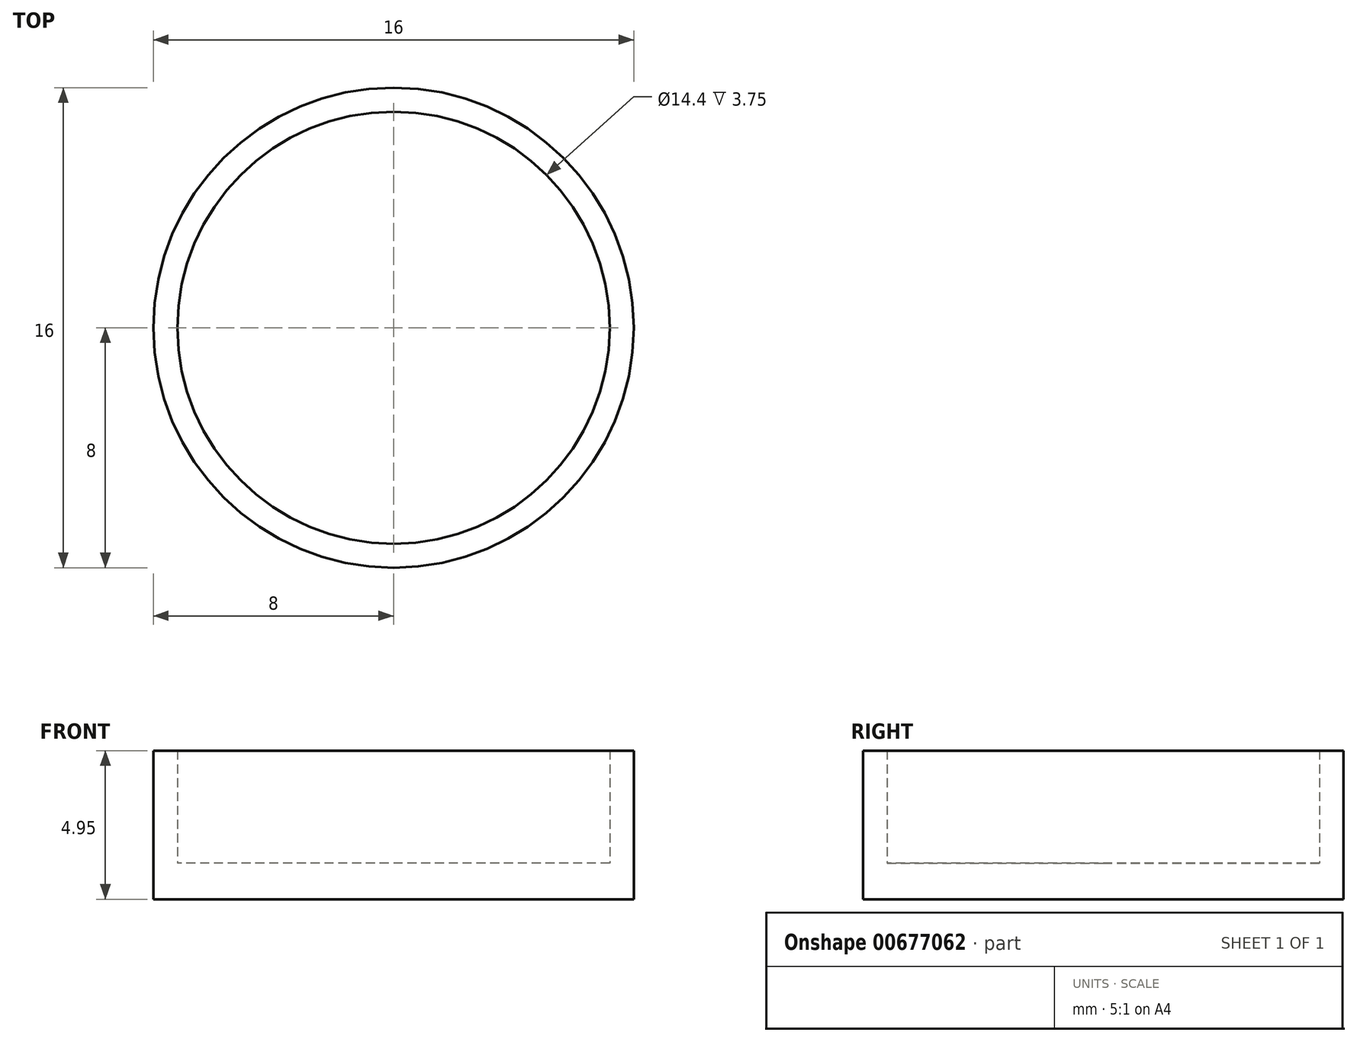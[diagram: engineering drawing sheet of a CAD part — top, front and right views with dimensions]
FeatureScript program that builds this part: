
annotation { "Feature Type Name" : "Feature", "Feature Type Description" : "" }
export const myFeature = defineFeature(function(context is Context, id is Id, definition is map)
    precondition{}
    {
        {
            var Q0;
            Q0=qCreatedBy(makeId("Top.planeOp"),FACE);
            var sketch = newSketch(context, id + "F0", { "sketchPlane" : qUnion([Q0])});
            skCircle(sketch, "E0", {"center": v(0, 0) * mm, "radius": 7.2 * mm});
            skCircle(sketch, "E1", {"center": v(0, 0) * mm, "radius": 8 * mm});
            skSolve(sketch);
        }
        {
            var Q0;
            Q0=makeQuery(id+"F0.imprint","IMPRINT",FACE,{"disambiguationData":[TD([[makeQuery(id+"F0.imprint","IMPRINT",EDGE,{"derivedFrom":sQuery(id+"F0.wireOp",EDGE,"E0")}),1.0]])]});
            extrude(context, id + "F1", {"entities" : qUnion([Q0]), "depth" : 1.2 * mm, "offsetDistance" : 25 * mm});
        }
        {
            var Q0;
            Q0=makeQuery(id+"F0.imprint","IMPRINT",FACE,{"disambiguationData":[TD([[makeQuery(id+"F0.imprint","IMPRINT",EDGE,{"derivedFrom":sQuery(id+"F0.wireOp",EDGE,"E0")}),-1.0]])]});
            extrude(context, id + "F2", {"entities" : qUnion([Q0]), "operationType" : NewBodyOperationType.ADD, "depth" : (1.2 + 3.75) * mm, "offsetDistance" : 25 * mm});
        }
    });
